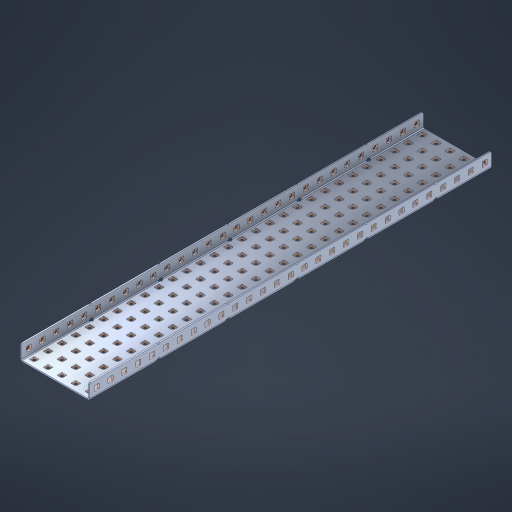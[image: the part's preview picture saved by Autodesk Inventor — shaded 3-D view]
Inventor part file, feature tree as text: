
AUTODESK INVENTOR PART (.ipt)
format: ipt  version: 2023 (Build 270158000, 158)  size: 2,216,960 bytes
history: native  units: in
note: dims shown in document units (in); Inventor stores cm internally (conversion verified against a paired STEP export)
features: other x208, extrude x202, sheet_metal_op x10, sketch x8, mirror x1, pattern_linear x1, chamfer x1
ambient origin geometry x8: Origin, YZ Plane, XZ Plane, XY Plane, X Axis, Y Axis, Z Axis, Center Point
bodies: Solid1 (feature_tree), Body (feature_tree)
feature tree (431):
  other  "Flange Pattern Plane"
  sheet_metal_op  "Flange Pattern"
  sheet_metal_op  "Body Pattern"
  other  "Arc Length"
  mirror  "Notch Mirror"
  pattern_linear  "Notch Pattern"  Spacing1=0.1875in  [1 undecoded]
  chamfer  "End Chamfer"
  extrude  "Half Cut"  Depth=0.0469in
  sketch  "Sketch1"  dims[d0=2.5in]
  other  "Plate1"
  sketch  "Sketch2"  dims[d1=14.5in]
  other  "Plate2"
  sheet_metal_op  "Bend1"
  sheet_metal_op  "Corner1"
  sketch  "Sketch3"  dims[d2=0.0469in]
  other  "Flange Pattern Sketch"
  sketch  "Sketch7"  dims[d3=0.0469in]
  other  "Srf1"
  other  "Srf2"
  sketch  "Sketch8"  dims[d4=0.0234in]
  sketch  "Sketch9"  dims[d5=0.0938in]
  other  "Srf91"
  sheet_metal_op  "Body Pattern Sketch"
  other  "Srf92"
  sketch  "Sketch13"  dims[d6=0.0469in]
  sketch  "Sketch14"  dims[d7=0.5in d8=90.0deg d9=0.0312in d10=0.1875in d11=0.0469in d12=0.0469in d16=0.182in d17=0.02in d18=0.0469in d19=0.0in d20=0.25in d21=0.25in d46=0.172in d47=1.0in d48=0.0in d49=0.182in d50=0.02in d51=0.25in d52=0.25in d53=0.0469in d54=0.0in d55=0.172in d56=1.0in d57=0.0in d60=11.4173in d62=0.5in d63=1.9685in d65=0.5in d85=0.1227in d86=0.1659in d88=0.04in d89=0.0469in d90=0.0in d91=0.04in d92=0.0491in d95=2.5in d96=0.04in d97=0.25in d98=45.0deg d101=0.0in d102=2.497in d131=2.5in d132=11.4173in d134=0.5in d139=0.5in]
  other  "Srf856"
  other  "Srf1310"
  other  "Srf1311"
  other  "Srf1312"
  other  "Srf1376"
  other  "Srf1377"
  other  "Srf1728"
  other  "Srf1755"
  other  "Srf1878"
  other  "Srf1879"
  other  "Srf1880"
  other  "Srf1881"
  other  "Srf1882"
  other  "Srf1883"
  other  "Srf1884"
  other  "Srf1885"
  other  "Srf1886"
  other  "Srf1887"
  other  "Srf1888"
  other  "Srf1889"
  other  "Srf1890"
  other  "Srf1891"
  other  "Srf1892"
  other  "Srf1893"
  other  "Srf1894"
  other  "Srf1895"
  other  "Srf1896"
  other  "Srf1897"
  other  "Srf1898"
  other  "Srf1899"
  other  "Srf1900"
  other  "Srf1901"
  other  "Srf1902"
  other  "Srf1903"
  other  "Srf1904"
  other  "Srf1905"
  other  "Srf1906"
  other  "Srf1942"
  other  "Srf1943"
  other  "Srf1944"
  other  "Srf1945"
  other  "Srf1946"
  other  "Srf1947"
  other  "Srf1948"
  other  "Srf1949"
  other  "Srf1950"
  other  "Srf1951"
  other  "Srf1952"
  other  "Srf1953"
  other  "Srf1954"
  other  "Srf1955"
  other  "Srf1956"
  other  "Srf1957"
  other  "Srf1958"
  other  "Srf1959"
  other  "Srf1960"
  other  "Srf1961"
  other  "Srf1962"
  other  "Srf1963"
  other  "Srf1964"
  other  "Srf1965"
  other  "Srf1966"
  other  "Srf1967"
  other  "Srf1968"
  other  "Srf1969"
  other  "Srf1970"
  other  "Srf2111"
  other  "Srf2112"
  other  "Srf2113"
  other  "Srf2114"
  other  "Srf2115"
  other  "Srf2116"
  other  "Srf2117"
  other  "Srf2118"
  other  "Srf2119"
  other  "Srf2120"
  other  "Srf2121"
  other  "Srf2122"
  other  "Srf2123"
  other  "Srf2124"
  other  "Srf2125"
  other  "Srf2126"
  other  "Srf2127"
  other  "Srf2128"
  other  "Srf2129"
  other  "Srf2130"
  other  "Srf2131"
  other  "Srf2132"
  other  "Srf2133"
  other  "Srf2146"
  other  "Srf2147"
  other  "Srf2148"
  other  "Srf2149"
  other  "Srf2150"
  other  "Srf2151"
  other  "Srf2152"
  other  "Srf2153"
  other  "Srf2154"
  other  "Srf2155"
  other  "Srf2156"
  other  "Srf2157"
  other  "Srf2158"
  other  "Srf2159"
  other  "Srf2160"
  other  "Srf2161"
  other  "Srf2162"
  other  "Srf2163"
  other  "Srf2164"
  other  "Srf2165"
  other  "Srf2166"
  other  "Srf2167"
  other  "Srf2168"
  other  "Srf2169"
  other  "Srf2170"
  other  "Srf2171"
  other  "Srf2172"
  other  "Srf2173"
  other  "Srf2174"
  other  "Srf2175"
  other  "Srf2176"
  other  "Srf2177"
  other  "Srf2178"
  other  "Srf2179"
  other  "Srf2180"
  other  "Srf2181"
  other  "Srf2182"
  other  "Srf2183"
  other  "Srf2184"
  other  "Srf2185"
  other  "Srf2186"
  other  "Srf2187"
  other  "Srf2188"
  other  "Srf2189"
  other  "Srf2190"
  other  "Srf2191"
  other  "Srf2192"
  other  "Srf2193"
  other  "Srf2194"
  other  "Srf2195"
  other  "Srf2196"
  other  "Srf2197"
  other  "Srf2198"
  other  "Srf2199"
  other  "Srf2200"
  other  "Srf2201"
  other  "Srf2202"
  other  "Srf2203"
  other  "Srf2204"
  other  "Srf2205"
  other  "Srf2206"
  other  "Srf2207"
  other  "Srf2208"
  other  "Srf2209"
  other  "Srf2210"
  other  "Srf2211"
  other  "Srf2212"
  other  "Srf2213"
  other  "Srf2214"
  other  "Srf2215"
  other  "Srf2216"
  other  "Srf2217"
  other  "Srf2218"
  other  "Srf2219"
  other  "Srf2220"
  other  "Srf2221"
  other  "Srf2222"
  other  "Srf2223"
  other  "Srf2224"
  other  "Srf2225"
  other  "Srf2226"
  other  "Srf2227"
  other  "Srf2228"
  other  "Srf2229"
  other  "Srf2230"
  other  "Srf2231"
  other  "Srf2232"
  other  "Srf2233"
  other  "Srf2234"
  other  "Srf2235"
  other  "Srf2236"
  other  "Srf2237"
  other  "Srf2238"
  other  "Srf2239"
  other  "Srf2240"
  other  "Srf2241"
  other  "Srf2242"
  other  "Srf2243"
  other  "Srf2244"
  other  "Srf2245"
  other  "Srf2246"
  other  "Srf2247"
  other  "Srf2248"
  other  "Srf2249"
  other  "Srf2250"
  other  "Srf2251"
  other  "Srf2252"
  other  "Srf2253"
  other  "Srf2254"
  other  "Srf2255"
  sheet_metal_op  "Flange Stamp"
  sheet_metal_op  "Flange Circle"
  sheet_metal_op  "Body Stamp"
  sheet_metal_op  "Body Circle"
  sheet_metal_op  "Notch"
  extrude  "ExtrusionSrf2"  Depth=0.0469in
  extrude  "ExtrusionSrf92"  Depth=2.5in
  extrude  "ExtrusionSrf856"  Depth=0.02in
  extrude  "ExtrusionSrf1310"  Depth=0.0469in
  extrude  "ExtrusionSrf1311"  TaperAngle=0.0deg  [1 undecoded]
  extrude  "ExtrusionSrf1312"  Depth=0.25in
  extrude  "ExtrusionSrf1376"  Depth=0.25in
  extrude  "ExtrusionSrf1377"  Depth=2.5in
  extrude  "ExtrusionSrf1728"  Depth=2.5in TaperAngle=0.0deg
  extrude  "ExtrusionSrf1755"  Depth=2.5in
  extrude  "ExtrusionSrf1878"  Depth=0.02in
  extrude  "ExtrusionSrf1879"  Depth=0.25in
  extrude  "ExtrusionSrf1880"  Depth=0.25in
  extrude  "ExtrusionSrf1881"  Depth=0.0469in
  extrude  "ExtrusionSrf1882"  TaperAngle=0.0deg  [1 undecoded]
  extrude  "ExtrusionSrf1883"  Depth=2.5in
  extrude  "ExtrusionSrf1884"  Depth=2.5in TaperAngle=0.0deg
  extrude  "ExtrusionSrf1885"  Depth=2.5in
  extrude  "ExtrusionSrf1886"  Depth=2.5in
  extrude  "ExtrusionSrf1887"  Depth=2.5in
  extrude  "ExtrusionSrf1888"  Depth=2.5in
  extrude  "ExtrusionSrf1889"  Depth=2.5in
  extrude  "ExtrusionSrf1890"  Depth=0.0469in
  extrude  "ExtrusionSrf1891"  TaperAngle=0.0deg  [1 undecoded]
  extrude  "ExtrusionSrf1892"  Depth=2.5in
  extrude  "ExtrusionSrf1893"  Depth=2.5in
  extrude  "ExtrusionSrf1894"  Depth=2.5in
  extrude  "ExtrusionSrf1895"  Depth=0.25in TaperAngle=45.0deg
  extrude  "ExtrusionSrf1896"  TaperAngle=0.0deg  [1 undecoded]
  extrude  "ExtrusionSrf1897"  Depth=2.5in
  extrude  "ExtrusionSrf1898"  Depth=2.5in
  extrude  "ExtrusionSrf1899"  Depth=2.5in
  extrude  "ExtrusionSrf1900"  Depth=2.5in
  extrude  "ExtrusionSrf1901"  Depth=2.5in
  extrude  "ExtrusionSrf1902"  [1 undecoded]
  extrude  "ExtrusionSrf1903"  [1 undecoded]
  extrude  "ExtrusionSrf1904"  [1 undecoded]
  extrude  "ExtrusionSrf1905"  [1 undecoded]
  extrude  "ExtrusionSrf1906"  [1 undecoded]
  extrude  "ExtrusionSrf1942"  [1 undecoded]
  extrude  "ExtrusionSrf1943"  [1 undecoded]
  extrude  "ExtrusionSrf1944"  [1 undecoded]
  extrude  "ExtrusionSrf1945"  [1 undecoded]
  extrude  "ExtrusionSrf1946"  [1 undecoded]
  extrude  "ExtrusionSrf1947"  [1 undecoded]
  extrude  "ExtrusionSrf1948"  [1 undecoded]
  extrude  "ExtrusionSrf1949"  [1 undecoded]
  extrude  "ExtrusionSrf1950"  [1 undecoded]
  extrude  "ExtrusionSrf1951"  [1 undecoded]
  extrude  "ExtrusionSrf1952"  [1 undecoded]
  extrude  "ExtrusionSrf1953"  [1 undecoded]
  extrude  "ExtrusionSrf1954"  [1 undecoded]
  extrude  "ExtrusionSrf1955"  [1 undecoded]
  extrude  "ExtrusionSrf1956"  [1 undecoded]
  extrude  "ExtrusionSrf1957"  [1 undecoded]
  extrude  "ExtrusionSrf1958"  [1 undecoded]
  extrude  "ExtrusionSrf1959"  [1 undecoded]
  extrude  "ExtrusionSrf1960"  [1 undecoded]
  extrude  "ExtrusionSrf1961"  [1 undecoded]
  extrude  "ExtrusionSrf1962"  [1 undecoded]
  extrude  "ExtrusionSrf1963"  [1 undecoded]
  extrude  "ExtrusionSrf1964"  [1 undecoded]
  extrude  "ExtrusionSrf1965"  [1 undecoded]
  extrude  "ExtrusionSrf1966"  [1 undecoded]
  extrude  "ExtrusionSrf1967"  [1 undecoded]
  extrude  "ExtrusionSrf1968"  [1 undecoded]
  extrude  "ExtrusionSrf1969"  [1 undecoded]
  extrude  "ExtrusionSrf1970"  [1 undecoded]
  extrude  "ExtrusionSrf2111"  [1 undecoded]
  extrude  "ExtrusionSrf2112"  [1 undecoded]
  extrude  "ExtrusionSrf2113"  [1 undecoded]
  extrude  "ExtrusionSrf2114"  [1 undecoded]
  extrude  "ExtrusionSrf2115"  [1 undecoded]
  extrude  "ExtrusionSrf2116"  [1 undecoded]
  extrude  "ExtrusionSrf2117"  [1 undecoded]
  extrude  "ExtrusionSrf2118"  [1 undecoded]
  extrude  "ExtrusionSrf2119"  [1 undecoded]
  extrude  "ExtrusionSrf2120"  [1 undecoded]
  extrude  "ExtrusionSrf2121"  [1 undecoded]
  extrude  "ExtrusionSrf2122"  [1 undecoded]
  extrude  "ExtrusionSrf2123"  [1 undecoded]
  extrude  "ExtrusionSrf2124"  [1 undecoded]
  extrude  "ExtrusionSrf2125"  [1 undecoded]
  extrude  "ExtrusionSrf2126"  [1 undecoded]
  extrude  "ExtrusionSrf2127"  [1 undecoded]
  extrude  "ExtrusionSrf2128"  [1 undecoded]
  extrude  "ExtrusionSrf2129"  [1 undecoded]
  extrude  "ExtrusionSrf2130"  [1 undecoded]
  extrude  "ExtrusionSrf2131"  [1 undecoded]
  extrude  "ExtrusionSrf2132"  [1 undecoded]
  extrude  "ExtrusionSrf2133"  [1 undecoded]
  extrude  "ExtrusionSrf2146"  [1 undecoded]
  extrude  "ExtrusionSrf2147"  [1 undecoded]
  extrude  "ExtrusionSrf2148"  [1 undecoded]
  extrude  "ExtrusionSrf2149"  [1 undecoded]
  extrude  "ExtrusionSrf2150"  [1 undecoded]
  extrude  "ExtrusionSrf2151"  [1 undecoded]
  extrude  "ExtrusionSrf2152"  [1 undecoded]
  extrude  "ExtrusionSrf2153"  [1 undecoded]
  extrude  "ExtrusionSrf2154"  [1 undecoded]
  extrude  "ExtrusionSrf2155"  [1 undecoded]
  extrude  "ExtrusionSrf2156"  [1 undecoded]
  extrude  "ExtrusionSrf2157"  [1 undecoded]
  extrude  "ExtrusionSrf2158"  [1 undecoded]
  extrude  "ExtrusionSrf2159"  [1 undecoded]
  extrude  "ExtrusionSrf2160"  [1 undecoded]
  extrude  "ExtrusionSrf2161"  [1 undecoded]
  extrude  "ExtrusionSrf2162"  [1 undecoded]
  extrude  "ExtrusionSrf2163"  [1 undecoded]
  extrude  "ExtrusionSrf2164"  [1 undecoded]
  extrude  "ExtrusionSrf2165"  [1 undecoded]
  extrude  "ExtrusionSrf2166"  [1 undecoded]
  extrude  "ExtrusionSrf2167"  [1 undecoded]
  extrude  "ExtrusionSrf2168"  [1 undecoded]
  extrude  "ExtrusionSrf2169"  [1 undecoded]
  extrude  "ExtrusionSrf2170"  [1 undecoded]
  extrude  "ExtrusionSrf2171"  [1 undecoded]
  extrude  "ExtrusionSrf2172"  [1 undecoded]
  extrude  "ExtrusionSrf2173"  [1 undecoded]
  extrude  "ExtrusionSrf2174"  [1 undecoded]
  extrude  "ExtrusionSrf2175"  [1 undecoded]
  extrude  "ExtrusionSrf2176"  [1 undecoded]
  extrude  "ExtrusionSrf2177"  [1 undecoded]
  extrude  "ExtrusionSrf2178"  [1 undecoded]
  extrude  "ExtrusionSrf2179"  [1 undecoded]
  extrude  "ExtrusionSrf2180"  [1 undecoded]
  extrude  "ExtrusionSrf2181"  [1 undecoded]
  extrude  "ExtrusionSrf2182"  [1 undecoded]
  extrude  "ExtrusionSrf2183"  [1 undecoded]
  extrude  "ExtrusionSrf2184"  [1 undecoded]
  extrude  "ExtrusionSrf2185"  [1 undecoded]
  extrude  "ExtrusionSrf2186"  [1 undecoded]
  extrude  "ExtrusionSrf2187"  [1 undecoded]
  extrude  "ExtrusionSrf2188"  [1 undecoded]
  extrude  "ExtrusionSrf2189"  [1 undecoded]
  extrude  "ExtrusionSrf2190"  [1 undecoded]
  extrude  "ExtrusionSrf2191"  [1 undecoded]
  extrude  "ExtrusionSrf2192"  [1 undecoded]
  extrude  "ExtrusionSrf2193"  [1 undecoded]
  extrude  "ExtrusionSrf2194"  [1 undecoded]
  extrude  "ExtrusionSrf2195"  [1 undecoded]
  extrude  "ExtrusionSrf2196"  [1 undecoded]
  extrude  "ExtrusionSrf2197"  [1 undecoded]
  extrude  "ExtrusionSrf2198"  [1 undecoded]
  extrude  "ExtrusionSrf2199"  [1 undecoded]
  extrude  "ExtrusionSrf2200"  [1 undecoded]
  extrude  "ExtrusionSrf2201"  [1 undecoded]
  extrude  "ExtrusionSrf2202"  [1 undecoded]
  extrude  "ExtrusionSrf2203"  [1 undecoded]
  extrude  "ExtrusionSrf2204"  [1 undecoded]
  extrude  "ExtrusionSrf2205"  [1 undecoded]
  extrude  "ExtrusionSrf2206"  [1 undecoded]
  extrude  "ExtrusionSrf2207"  [1 undecoded]
  extrude  "ExtrusionSrf2208"  [1 undecoded]
  extrude  "ExtrusionSrf2209"  [1 undecoded]
  extrude  "ExtrusionSrf2210"  [1 undecoded]
  extrude  "ExtrusionSrf2211"  [1 undecoded]
  extrude  "ExtrusionSrf2212"  [1 undecoded]
  extrude  "ExtrusionSrf2213"  [1 undecoded]
  extrude  "ExtrusionSrf2214"  [1 undecoded]
  extrude  "ExtrusionSrf2215"  [1 undecoded]
  extrude  "ExtrusionSrf2216"  [1 undecoded]
  extrude  "ExtrusionSrf2217"  [1 undecoded]
  extrude  "ExtrusionSrf2218"  [1 undecoded]
  extrude  "ExtrusionSrf2219"  [1 undecoded]
  extrude  "ExtrusionSrf2220"  [1 undecoded]
  extrude  "ExtrusionSrf2221"  [1 undecoded]
  extrude  "ExtrusionSrf2222"  [1 undecoded]
  extrude  "ExtrusionSrf2223"  [1 undecoded]
  extrude  "ExtrusionSrf2224"  [1 undecoded]
  extrude  "ExtrusionSrf2225"  [1 undecoded]
  extrude  "ExtrusionSrf2226"  [1 undecoded]
  extrude  "ExtrusionSrf2227"  [1 undecoded]
  extrude  "ExtrusionSrf2228"  [1 undecoded]
  extrude  "ExtrusionSrf2229"  [1 undecoded]
  extrude  "ExtrusionSrf2230"  [1 undecoded]
  extrude  "ExtrusionSrf2231"  [1 undecoded]
  extrude  "ExtrusionSrf2232"  [1 undecoded]
  extrude  "ExtrusionSrf2233"  [1 undecoded]
  extrude  "ExtrusionSrf2234"  [1 undecoded]
  extrude  "ExtrusionSrf2235"  [1 undecoded]
  extrude  "ExtrusionSrf2236"  [1 undecoded]
  extrude  "ExtrusionSrf2237"  [1 undecoded]
  extrude  "ExtrusionSrf2238"  [1 undecoded]
  extrude  "ExtrusionSrf2239"  [1 undecoded]
  extrude  "ExtrusionSrf2240"  [1 undecoded]
  extrude  "ExtrusionSrf2241"  [1 undecoded]
  extrude  "ExtrusionSrf2242"  [1 undecoded]
  extrude  "ExtrusionSrf2243"  [1 undecoded]
  extrude  "ExtrusionSrf2244"  [1 undecoded]
  extrude  "ExtrusionSrf2245"  [1 undecoded]
  extrude  "ExtrusionSrf2246"  [1 undecoded]
  extrude  "ExtrusionSrf2247"  [1 undecoded]
  extrude  "ExtrusionSrf2248"  [1 undecoded]
  extrude  "ExtrusionSrf2249"  [1 undecoded]
  extrude  "ExtrusionSrf2250"  [1 undecoded]
  extrude  "ExtrusionSrf2251"  [1 undecoded]
  extrude  "ExtrusionSrf2252"  [1 undecoded]
  extrude  "ExtrusionSrf2253"  [1 undecoded]
  extrude  "ExtrusionSrf2254"  [1 undecoded]
  extrude  "ExtrusionSrf2255"  [1 undecoded]
note: 172 required parameter values undecoded (feature->parameter linkage not recoverable at this tier; creation-order binding heuristic only, values carry confidence <= 0.55)
